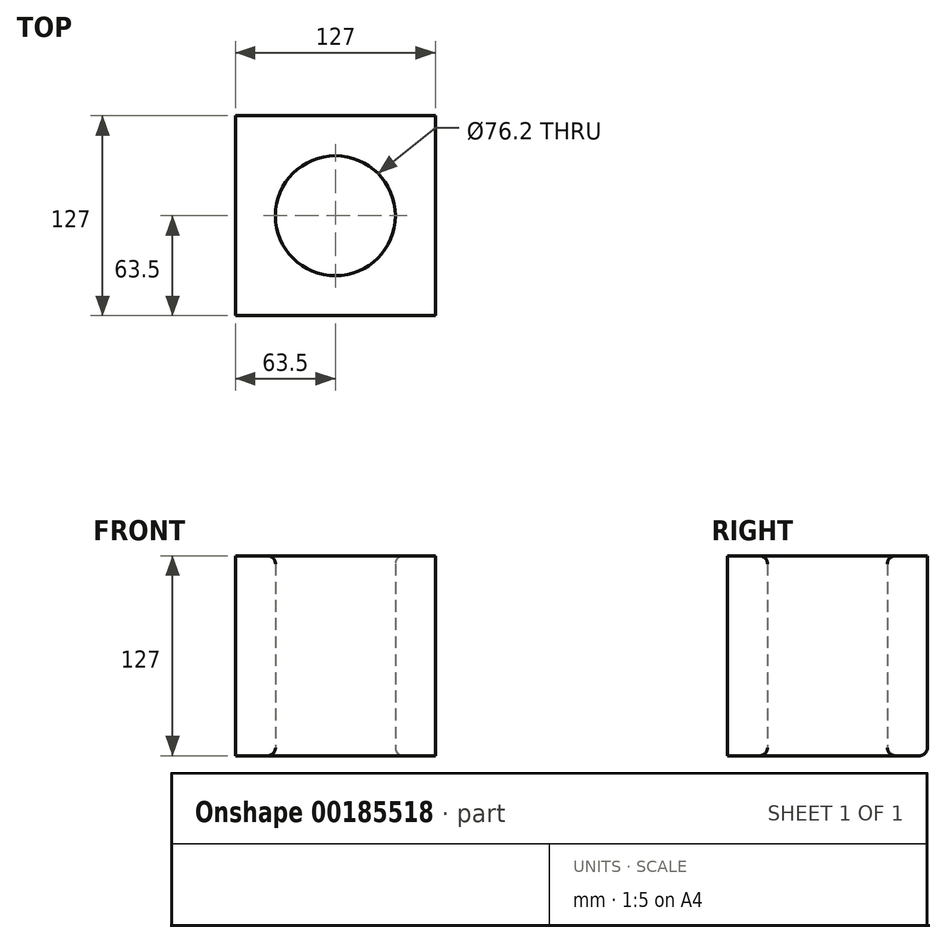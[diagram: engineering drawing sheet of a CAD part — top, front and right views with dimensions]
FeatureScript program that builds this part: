
annotation { "Feature Type Name" : "Feature", "Feature Type Description" : "" }
export const myFeature = defineFeature(function(context is Context, id is Id, definition is map)
    precondition{}
    {
        {
            var Q0;
            Q0=qCreatedBy(makeId("Front.planeOp"),FACE);
            var sketch = newSketch(context, id + "F0", { "sketchPlane" : qUnion([Q0])});
            skLineSegment(sketch, "E0.bottom", {"start": v(-63.5, 41.72) * mm, "end": v(63.5, 41.72) * mm});
            skLineSegment(sketch, "E0.top", {"start": v(-63.5, -85.28) * mm, "end": v(63.5, -85.28) * mm});
            skLineSegment(sketch, "E0.left", {"start": v(-63.5, 41.72) * mm, "end": v(-63.5, -85.28) * mm});
            skLineSegment(sketch, "E0.right", {"start": v(63.5, 41.72) * mm, "end": v(63.5, -85.28) * mm});
            skSolve(sketch);
        }
        {
            var Q0;
            Q0 = qSketchRegion(id + "F0", true);
            extrude(context, id + "F1", {"entities" : qUnion([Q0]), "depth" : 127 * mm});
        }
        {
            var Q0;
            Q0=makeQuery(id+"F1.opExtrude","SWEPT_FACE",FACE,{"disambiguationData":[OSD([sQuery(id+"F0.wireOp",EDGE,"E0.top")])]});
            var sketch = newSketch(context, id + "F2", { "sketchPlane" : qUnion([Q0])});
            skLineSegment(sketch, "E1", {"start": v(-63.5, 127) * mm, "end": v(63.5, 0) * mm, "construction": true});
            skCircle(sketch, "E2", {"center": v(0, 63.5) * mm, "radius": 38.1 * mm});
            skSolve(sketch);
        }
        {
            var Q0;
            Q0 = qSketchRegion(id + "F2", true);
            extrude(context, id + "F3", {"entities" : qUnion([Q0]), "operationType" : NewBodyOperationType.REMOVE, "endBound" : BoundingType.THROUGH_ALL, "oppositeDirection" : true, "depth" : 25.4 * mm});
        }
        {
            var Q0;
            Q0=makeQuery(id+"F3.boolean.opBoolean","COPY",FACE,{"derivedFrom":makeQuery(id+"F3.opExtrude","SWEPT_FACE",FACE,{"disambiguationData":[OSD([sQuery(id+"F2.wireOp",EDGE,"E2")])]})});
            var Q1;
            Q1=makeQuery(id+"F3.boolean.opBoolean","COPY",EDGE,{"derivedFrom":makeQuery(id+"F3.opExtrude","CAP_EDGE",EDGE,{"disambiguationData":[OSD([sQuery(id+"F2.wireOp",EDGE,"E2")])],"isStart":true})});
            var Q2;
            Q2=makeQuery(id+"F1.opExtrude","CAP_EDGE",EDGE,{"disambiguationData":[OSD([sQuery(id+"F0.wireOp",EDGE,"E0.top")])],"isStart":true});
            fillet(context, id + "F4", {"entities" : qUnion([Q0, Q1, Q2]), "radius" : 5.08 * mm, "tangentPropagation" : true, "allowEdgeOverflow" : false});
        }
    });
